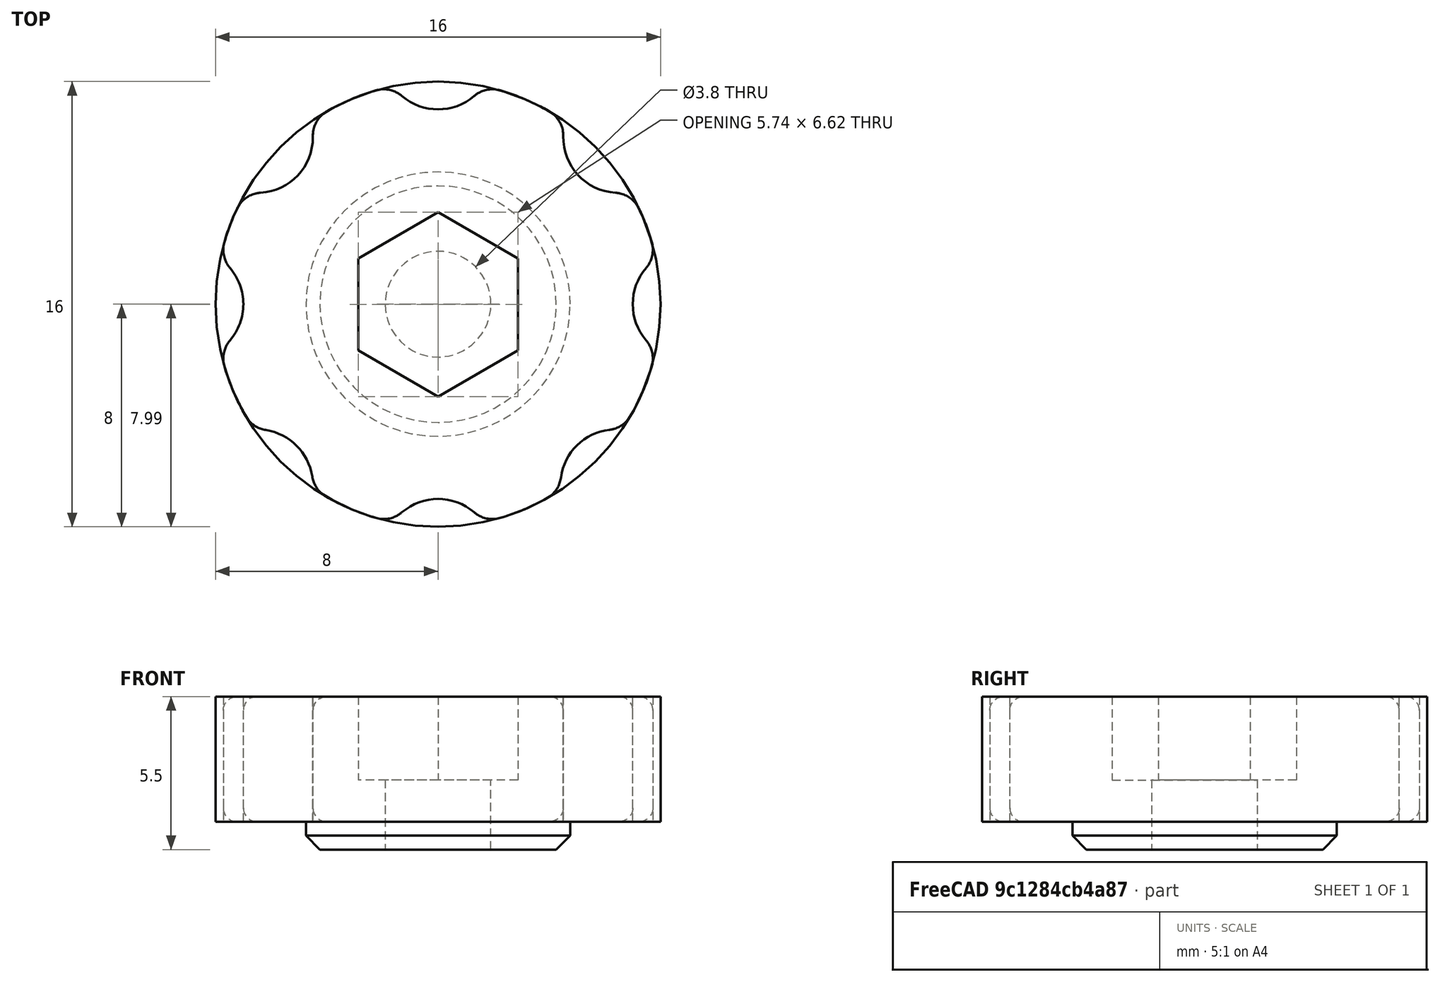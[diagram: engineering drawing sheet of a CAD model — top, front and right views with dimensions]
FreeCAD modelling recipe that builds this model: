
FCSTD DOCUMENT  (FreeCAD 0.15R4671 (Git))
Label: BedLevelingKnob
License: All rights reserved
LicenseURL: http://en.wikipedia.org/wiki/All_rights_reserved
objects: Sketcher::SketchObject×5, PartDesign::Pocket×3, PartDesign::Pad×2, PartDesign::Fillet×2, Mesh::Feature×1, PartDesign::Chamfer×1
note: 18 computed .brp shape members not serialized (recipe doc carries the construction recipe); baked Part::Feature solids carry a one-line shape summary decoded from their .brp

FEATURE [Mesh::Feature] HexNutStyle1_M3
  Placement = pos=(14.21,22,-114.55) rot=(0,0,1;0rad)
FEATURE [Sketcher::SketchObject] Sketch
  sketch-geometry (1):
    g0: Circle CenterX=0 CenterY=0 CenterZ=0 NormalX=0 NormalY=0 NormalZ=1 Radius=8
  constraints (2):
    c: Coincident(g0,g-1)
    c: Radius(g0) = 8
FEATURE [PartDesign::Pad] Pad
  Length = 4.5
  Length2 = 100
  Sketch = -> Sketch
  Type = 0
FEATURE [Sketcher::SketchObject] Sketch001
  Placement = pos=(0,0,4.5) rot=(0,0,1;0rad)
  Support = -> Pad [Face3]
  sketch-geometry (8):
    g0: Circle CenterX=0 CenterY=9 CenterZ=0 NormalX=0 NormalY=0 NormalZ=1 Radius=2
    g1: Circle CenterX=0 CenterY=-9 CenterZ=0 NormalX=0 NormalY=0 NormalZ=1 Radius=2
    g2: Circle CenterX=9 CenterY=0 CenterZ=0 NormalX=0 NormalY=0 NormalZ=1 Radius=2
    g3: Circle CenterX=-9 CenterY=0 CenterZ=0 NormalX=0 NormalY=0 NormalZ=1 Radius=2
    g4: Circle CenterX=-6.5 CenterY=6 CenterZ=0 NormalX=0 NormalY=0 NormalZ=1 Radius=2
    g5: Circle CenterX=6.39893 CenterY=-6.5 CenterZ=0 NormalX=0 NormalY=0 NormalZ=1 Radius=2
    g6: Circle CenterX=6.5 CenterY=6 CenterZ=0 NormalX=0 NormalY=0 NormalZ=1 Radius=2
    g7: Circle CenterX=-6.5 CenterY=-6.5 CenterZ=0 NormalX=0 NormalY=0 NormalZ=1 Radius=2
  constraints (9):
    c: PointOnObject(g0,g-2)
    c: Radius(g0) = 2
    c: Equal(g0,g6)
    c: Equal(g0,g2)
    c: Equal(g0,g5)
    c: Equal(g0,g1)
    c: Equal(g0,g7)
    c: Equal(g0,g3)
    c: Equal(g0,g4)
FEATURE [PartDesign::Pocket] Pocket
  Length = 5
  Sketch = -> Sketch001
  Type = 1
FEATURE [PartDesign::Fillet] Fillet
  Base = -> Pocket [Edge50,Edge52,Edge53,Edge54,Edge42,Edge4,Edge51,Edge48,Edge49,Edge46,Edge47,Edge45,Edge44,Edge43,Edge24,Edge2]
  Radius = 1
FEATURE [Sketcher::SketchObject] Sketch002
  Placement = pos=(0,0,4.5) rot=(0,0,1;0rad)
  Support = -> Fillet [Face5]
  sketch-geometry (7):
    g0: LineSegment StartX=0 StartY=3.3021 StartZ=0 EndX=-2.86787 EndY=1.64634 EndZ=0
    g1: LineSegment StartX=-2.86787 StartY=1.64634 StartZ=0 EndX=-2.86787 EndY=-1.66519 EndZ=0
    g2: LineSegment StartX=-2.86787 StartY=-1.66519 StartZ=0 EndX=0 EndY=-3.32096 EndZ=0
    g3: LineSegment StartX=0 StartY=-3.32096 StartZ=0 EndX=2.86787 EndY=-1.66519 EndZ=0
    g4: LineSegment StartX=2.86787 StartY=-1.66519 StartZ=0 EndX=2.86787 EndY=1.64634 EndZ=0
    g5: LineSegment StartX=2.86787 StartY=1.64634 StartZ=0 EndX=0 EndY=3.3021 EndZ=0
    g6: Circle [constr] CenterX=0 CenterY=-0.00942781 CenterZ=0 NormalX=0 NormalY=0 NormalZ=1 Radius=3.31153
  constraints (15):
    c: Coincident(g0,g1)
    c: Coincident(g1,g2)
    c: Coincident(g2,g3)
    c: Coincident(g3,g4)
    c: Coincident(g4,g5)
    c: Coincident(g5,g0)
    c: Equal(g0, g1-g5) x5
    c: PointOnObject(g0,g6)
    c: PointOnObject(g1,g6)
    c: PointOnObject(g2,g6)
    c: PointOnObject(g3,g6)
    c: PointOnObject(g4,g6)
    c: PointOnObject(g5,g6)
    c: Coincident(g3,g-1)
    c: Vertical(g4)
FEATURE [PartDesign::Pocket] Pocket001
  Length = 3
  Sketch = -> Sketch002
  Type = 0
FEATURE [Sketcher::SketchObject] Sketch003
  Placement = pos=(0,0,0) rot=(1,0,0;3.14159rad)
  Support = -> Pocket001 [Face2]
  sketch-geometry (1):
    g0: Circle CenterX=0 CenterY=0 CenterZ=0 NormalX=0 NormalY=0 NormalZ=1 Radius=4.75
  constraints (1):
    c: Coincident(g0,g-1)
FEATURE [PartDesign::Pad] Pad001
  Length = 1
  Length2 = 100
  Sketch = -> Sketch003
  Type = 0
FEATURE [PartDesign::Chamfer] Chamfer
  Base = -> Pad001 [Edge109]
  Size = 0.5
FEATURE [Sketcher::SketchObject] Sketch004
  Placement = pos=(0,0,-1) rot=(1,0,0;3.14159rad)
  Support = -> Chamfer [Face4]
  sketch-geometry (1):
    g0: Circle CenterX=0 CenterY=0 CenterZ=0 NormalX=0 NormalY=0 NormalZ=1 Radius=1.9
  constraints (2):
    c: Coincident(g0,g-1)
    c: Radius(g0) = 1.9
FEATURE [PartDesign::Pocket] Pocket002
  Length = 5
  Sketch = -> Sketch004
  Type = 1
FEATURE [PartDesign::Fillet] Fillet001  label="BedLevelingKnob"
  Base = -> Pocket002 [Edge70,Edge20]
  Radius = 0.5
